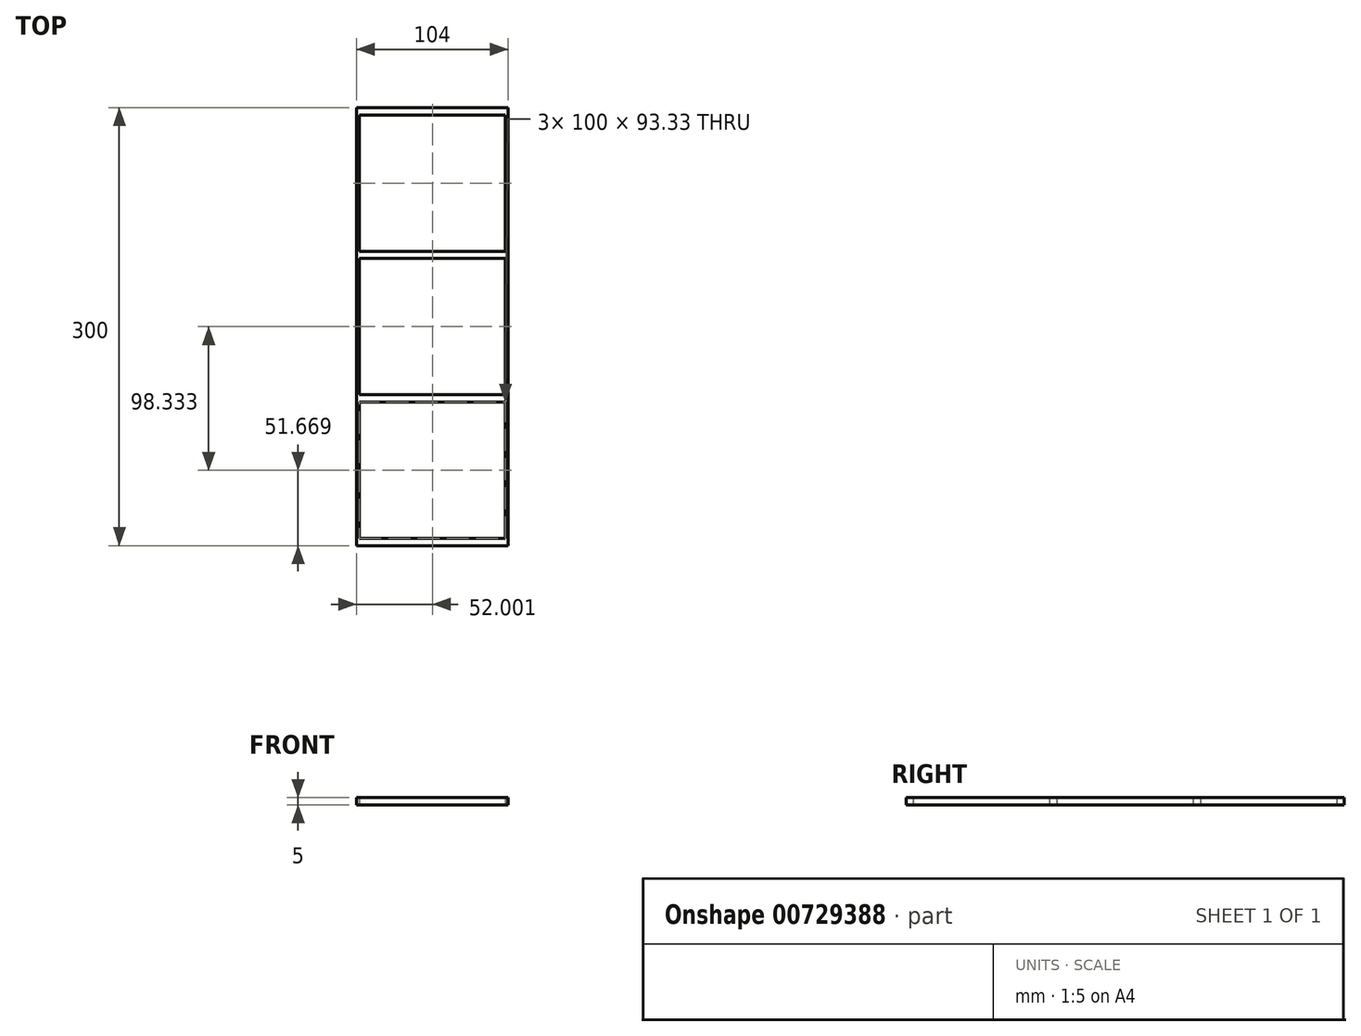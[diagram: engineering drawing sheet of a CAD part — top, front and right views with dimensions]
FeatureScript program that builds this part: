
annotation { "Feature Type Name" : "Feature", "Feature Type Description" : "" }
export const myFeature = defineFeature(function(context is Context, id is Id, definition is map)
    precondition{}
    {
        {
            var Q0;
            Q0=qCreatedBy(makeId("Top.planeOp"),FACE);
            var sketch = newSketch(context, id + "F0", { "sketchPlane" : qUnion([Q0])});
            skLineSegment(sketch, "E0", {"start": v(-135.04, 234.86) * mm, "end": v(-135.04, -65.14) * mm});
            skLineSegment(sketch, "E1", {"start": v(-135.04, -65.14) * mm, "end": v(-35.04, -65.14) * mm});
            skLineSegment(sketch, "E2", {"start": v(-35.04, -65.14) * mm, "end": v(-35.04, 234.86) * mm});
            skLineSegment(sketch, "E3", {"start": v(-35.04, 234.86) * mm, "end": v(-135.04, 234.86) * mm});
            skLineSegment(sketch, "E4", {"start": v(-135.04, 229.86) * mm, "end": v(-35.04, 229.86) * mm});
            skLineSegment(sketch, "E5", {"start": v(-135.04, 136.53) * mm, "end": v(-35.04, 136.53) * mm});
            skLineSegment(sketch, "E6", {"start": v(-135.04, 131.53) * mm, "end": v(-35.04, 131.53) * mm});
            skLineSegment(sketch, "E7", {"start": v(-135.04, 38.2) * mm, "end": v(-35.04, 38.2) * mm});
            skLineSegment(sketch, "E8", {"start": v(-135.04, 33.2) * mm, "end": v(-35.04, 33.2) * mm});
            skLineSegment(sketch, "E9", {"start": v(-135.04, -60.14) * mm, "end": v(-35.04, -60.14) * mm});
            skLineSegment(sketch, "E10", {"start": v(-135.04, 234.86) * mm, "end": v(-137.04, 234.86) * mm});
            skLineSegment(sketch, "E11", {"start": v(-137.04, 234.86) * mm, "end": v(-137.04, -65.14) * mm});
            skLineSegment(sketch, "E12", {"start": v(-137.04, -65.14) * mm, "end": v(-135.04, -65.14) * mm});
            skLineSegment(sketch, "E13", {"start": v(-35.04, 234.86) * mm, "end": v(-33.04, 234.86) * mm});
            skLineSegment(sketch, "E14", {"start": v(-33.04, 234.86) * mm, "end": v(-33.04, -65.14) * mm});
            skLineSegment(sketch, "E15", {"start": v(-33.04, -65.14) * mm, "end": v(-35.04, -65.14) * mm});
            skSolve(sketch);
        }
        {
            var Q0;
            {var subQ0=sQuery(id+"F0.wireOp",EDGE,"E1");Q0=makeQuery(id+"F0.imprint","IMPRINT",FACE,{"disambiguationData":[TD([[makeQuery(id+"F0.imprint","IMPRINT",EDGE,{"derivedFrom":subQ0}),1.0]])]});}
            var Q1;
            {var subQ0=sQuery(id+"F0.wireOp",EDGE,"E7");Q1=makeQuery(id+"F0.imprint","IMPRINT",FACE,{"disambiguationData":[TD([[makeQuery(id+"F0.imprint","IMPRINT",EDGE,{"derivedFrom":subQ0}),-1.0]])]});}
            var Q2;
            {var subQ0=sQuery(id+"F0.wireOp",EDGE,"E5");Q2=makeQuery(id+"F0.imprint","IMPRINT",FACE,{"disambiguationData":[TD([[makeQuery(id+"F0.imprint","IMPRINT",EDGE,{"derivedFrom":subQ0}),-1.0]])]});}
            var Q3;
            {var subQ0=sQuery(id+"F0.wireOp",EDGE,"E3");Q3=makeQuery(id+"F0.imprint","IMPRINT",FACE,{"disambiguationData":[TD([[makeQuery(id+"F0.imprint","IMPRINT",EDGE,{"derivedFrom":subQ0}),1.0]])]});}
            var Q4;
            {var subQ6=sQuery(id+"F0.wireOp",EDGE,"E10");Q4=makeQuery(id+"F0.imprint","IMPRINT",FACE,{"disambiguationData":[TD([[makeQuery(id+"F0.imprint","IMPRINT",EDGE,{"derivedFrom":subQ6}),1.0]])]});}
            var Q5;
            {var subQ8=sQuery(id+"F0.wireOp",EDGE,"E13");Q5=makeQuery(id+"F0.imprint","IMPRINT",FACE,{"disambiguationData":[TD([[makeQuery(id+"F0.imprint","IMPRINT",EDGE,{"derivedFrom":subQ8}),-1.0]])]});}
            extrude(context, id + "F1", {"entities" : qUnion([Q0, Q1, Q2, Q3, Q4, Q5]), "depth" : 5 * mm, "offsetDistance" : 25 * mm});
        }
    });
